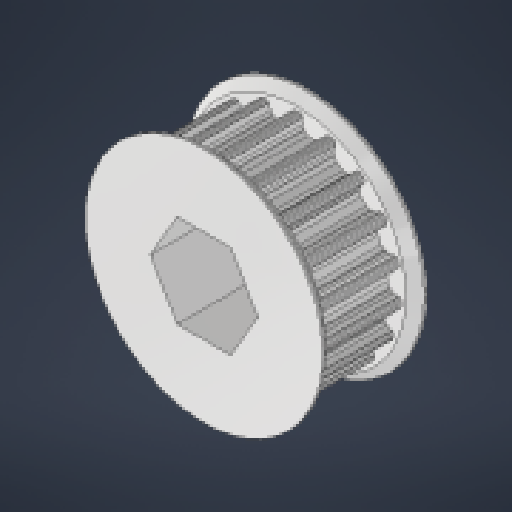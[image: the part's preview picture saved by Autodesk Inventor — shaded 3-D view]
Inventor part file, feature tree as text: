
AUTODESK INVENTOR PART (.ipt)
format: ipt  version: 2024.3 (Build 283343010, 343A)  size: 540,672 bytes
history: native  units: in
note: dims shown in document units (in); Inventor stores cm internally (conversion verified against a paired STEP export)
features: chamfer x1, other x1
ambient origin geometry x8: Origin, YZ Plane, XZ Plane, XY Plane, X Axis, Y Axis, Z Axis, Center Point
bodies: Solid1 (feature_tree)
feature tree (2):
  chamfer  "Chamfer1"  Distance=0.0492in Angle=45.0deg
  other  "Pulley"
